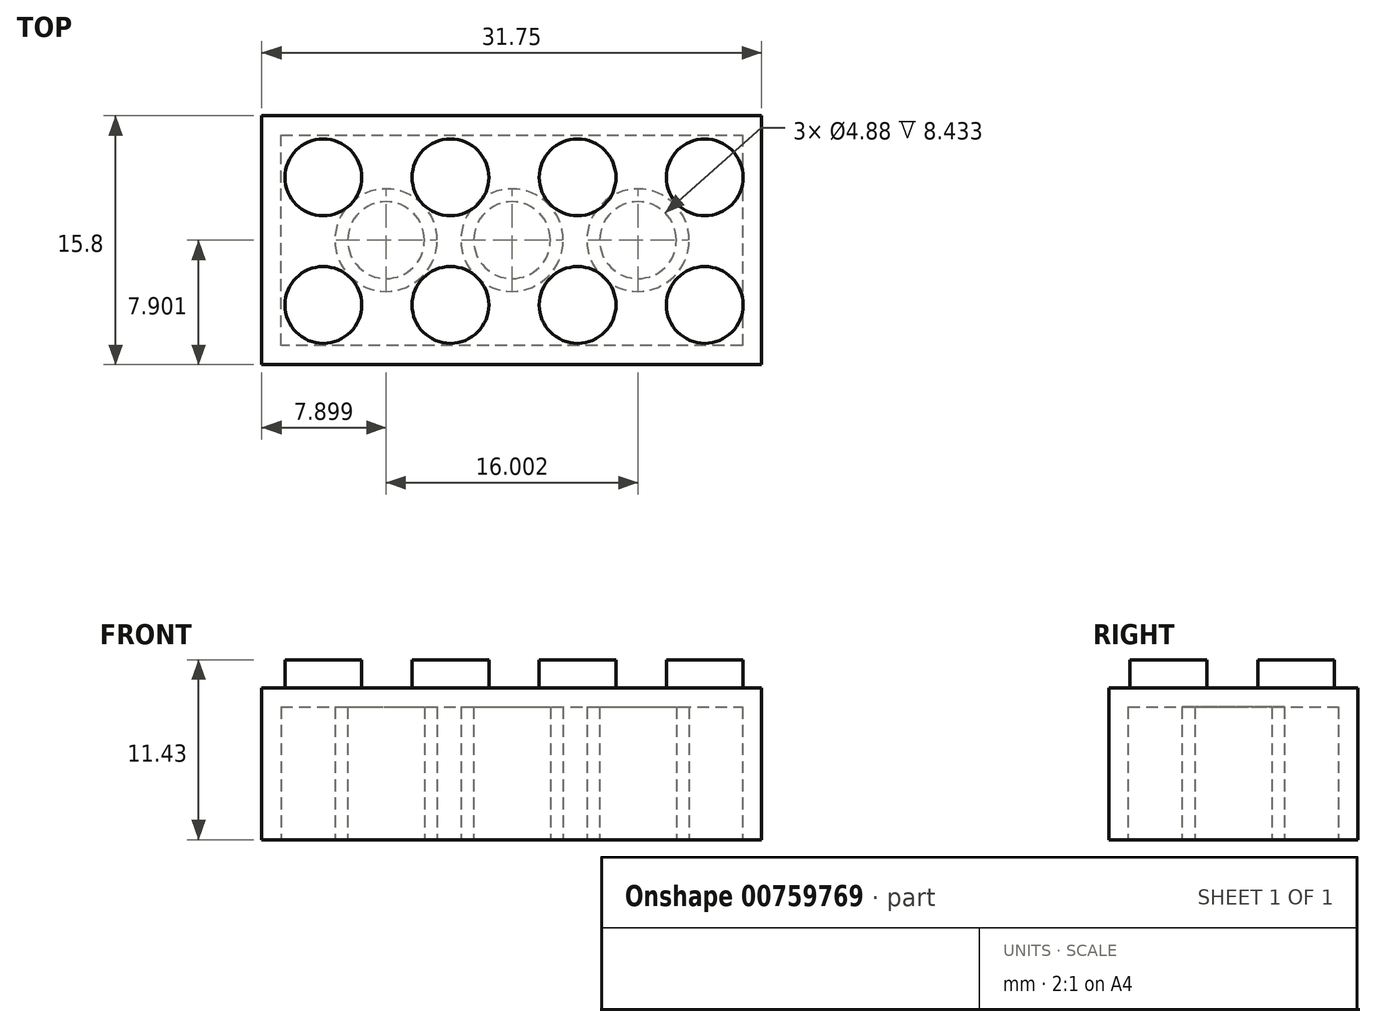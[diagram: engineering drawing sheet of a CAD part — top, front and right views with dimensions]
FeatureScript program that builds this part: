
annotation { "Feature Type Name" : "Feature", "Feature Type Description" : "" }
export const myFeature = defineFeature(function(context is Context, id is Id, definition is map)
    precondition{}
    {
        {
            var Q0;
            Q0=qCreatedBy(makeId("Front.planeOp"),FACE);
            var sketch = newSketch(context, id + "F0", { "sketchPlane" : qUnion([Q0])});
            skLineSegment(sketch, "E0.bottom", {"start": v(0, 0) * mm, "end": v(-31.75, 0) * mm});
            skLineSegment(sketch, "E0.top", {"start": v(0, -9.65) * mm, "end": v(-31.75, -9.65) * mm});
            skLineSegment(sketch, "E0.left", {"start": v(0, 0) * mm, "end": v(0, -9.65) * mm});
            skLineSegment(sketch, "E0.right", {"start": v(-31.75, 0) * mm, "end": v(-31.75, -9.65) * mm});
            skSolve(sketch);
        }
        {
            var Q0;
            Q0 = qSketchRegion(id + "F0", true);
            extrude(context, id + "F1", {"entities" : qUnion([Q0]), "depth" : 15.8 * mm, "offsetDistance" : 25.4 * mm});
        }
        {
            var Q0;
            Q0=makeQuery(id+"F1.opExtrude","SWEPT_FACE",FACE,{"disambiguationData":[OSD([sQuery(id+"F0.wireOp",EDGE,"E0.bottom")])]});
            var sketch = newSketch(context, id + "F2", { "sketchPlane" : qUnion([Q0])});
            skPoint(sketch, "E1.end.orphan", {"position": v(-27.4, 0) * mm});
            skPoint(sketch, "E2.orphan", {"position": v(-27.4, -3.6) * mm});
            skPoint(sketch, "E3.start.orphan", {"position": v(-17.14, -15.98) * mm});
            skPoint(sketch, "E4.orphan", {"position": v(-27.4, -9.8) * mm});
            skPoint(sketch, "E5.end.orphan", {"position": v(-27.4, -15.98) * mm});
            skLineSegment(sketch, "E6.0", {"start": v(0, 0) * mm, "end": v(-31.75, 0) * mm});
            skLineSegment(sketch, "E7.0", {"start": v(-31.75, -15.8) * mm, "end": v(-31.75, 0) * mm});
            skLineSegment(sketch, "E8.0", {"start": v(0, -15.8) * mm, "end": v(-31.75, -15.8) * mm});
            skLineSegment(sketch, "E9.0", {"start": v(0, -15.8) * mm, "end": v(0, 0) * mm});
            skLineSegment(sketch, "E10", {"start": v(-31.75, 0) * mm, "end": v(-27.84, 0) * mm, "construction": true});
            skLineSegment(sketch, "E11", {"start": v(-27.84, 0) * mm, "end": v(-27.84, -15.98) * mm, "construction": true});
            skLineSegment(sketch, "E12", {"start": v(-26.02, 0) * mm, "end": v(-26.02, -3.91) * mm, "construction": true});
            skLineSegment(sketch, "E13", {"start": v(-26.02, -3.91) * mm, "end": v(-31.75, -3.91) * mm, "construction": true});
            skLineSegment(sketch, "E14", {"start": v(-31.75, -3.91) * mm, "end": v(0, -3.91) * mm, "construction": true});
            skCircle(sketch, "E15", {"center": v(-27.84, -3.91) * mm, "radius": 2.44 * mm});
            skCircle(sketch, "E16.1.0.0", {"center": v(-19.76, -3.91) * mm, "radius": 2.44 * mm});
            skCircle(sketch, "E16.2.0.0", {"center": v(-11.68, -3.91) * mm, "radius": 2.44 * mm});
            skCircle(sketch, "E16.3.0.0", {"center": v(-3.6, -3.91) * mm, "radius": 2.44 * mm});
            skLineSegment(sketch, "E16.direction1", {"start": v(-27.84, -3.91) * mm, "end": v(-19.76, -3.91) * mm, "construction": true});
            skCircle(sketch, "E17.1.0.0", {"center": v(-27.84, -12.01) * mm, "radius": 2.44 * mm});
            skCircle(sketch, "E17.1.0.1", {"center": v(-19.76, -12.01) * mm, "radius": 2.44 * mm});
            skCircle(sketch, "E17.1.0.2", {"center": v(-11.68, -12.01) * mm, "radius": 2.44 * mm});
            skCircle(sketch, "E17.1.0.3", {"center": v(-3.6, -12.01) * mm, "radius": 2.44 * mm});
            skLineSegment(sketch, "E17.direction1", {"start": v(-27.84, -3.91) * mm, "end": v(-27.84, -12.01) * mm, "construction": true});
            skSolve(sketch);
        }
        {
            var Q0;
            Q0=makeQuery(id+"F2.imprint","IMPRINT",FACE,{"disambiguationData":[TD([[makeQuery(id+"F2.imprint","IMPRINT",EDGE,{"derivedFrom":sQuery(id+"F2.wireOp",EDGE,"E15")}),1.0]])]});
            var Q1;
            Q1=makeQuery(id+"F2.imprint","IMPRINT",FACE,{"disambiguationData":[TD([[makeQuery(id+"F2.imprint","IMPRINT",EDGE,{"derivedFrom":sQuery(id+"F2.wireOp",EDGE,"E16.1.0.0")}),1.0]])]});
            var Q2;
            Q2=makeQuery(id+"F2.imprint","IMPRINT",FACE,{"disambiguationData":[TD([[makeQuery(id+"F2.imprint","IMPRINT",EDGE,{"derivedFrom":sQuery(id+"F2.wireOp",EDGE,"E16.2.0.0")}),1.0]])]});
            var Q3;
            Q3=makeQuery(id+"F2.imprint","IMPRINT",FACE,{"disambiguationData":[TD([[makeQuery(id+"F2.imprint","IMPRINT",EDGE,{"derivedFrom":sQuery(id+"F2.wireOp",EDGE,"E16.3.0.0")}),1.0]])]});
            var Q4;
            Q4=makeQuery(id+"F2.imprint","IMPRINT",FACE,{"disambiguationData":[TD([[makeQuery(id+"F2.imprint","IMPRINT",EDGE,{"derivedFrom":sQuery(id+"F2.wireOp",EDGE,"E17.1.0.3")}),1.0]])]});
            var Q5;
            Q5=makeQuery(id+"F2.imprint","IMPRINT",FACE,{"disambiguationData":[TD([[makeQuery(id+"F2.imprint","IMPRINT",EDGE,{"derivedFrom":sQuery(id+"F2.wireOp",EDGE,"E17.1.0.2")}),1.0]])]});
            var Q6;
            Q6=makeQuery(id+"F2.imprint","IMPRINT",FACE,{"disambiguationData":[TD([[makeQuery(id+"F2.imprint","IMPRINT",EDGE,{"derivedFrom":sQuery(id+"F2.wireOp",EDGE,"E17.1.0.1")}),1.0]])]});
            var Q7;
            Q7=makeQuery(id+"F2.imprint","IMPRINT",FACE,{"disambiguationData":[TD([[makeQuery(id+"F2.imprint","IMPRINT",EDGE,{"derivedFrom":sQuery(id+"F2.wireOp",EDGE,"E17.1.0.0")}),1.0]])]});
            extrude(context, id + "F3", {"entities" : qUnion([Q0, Q1, Q2, Q3, Q4, Q5, Q6, Q7]), "operationType" : NewBodyOperationType.ADD, "depth" : 1.78 * mm, "offsetDistance" : 25.4 * mm});
        }
        {
            var Q0;
            Q0=makeQuery(id+"F1.opExtrude","SWEPT_FACE",FACE,{"disambiguationData":[OSD([sQuery(id+"F0.wireOp",EDGE,"E0.top")])]});
            var sketch = newSketch(context, id + "F4", { "sketchPlane" : qUnion([Q0])});
            skLineSegment(sketch, "E18.0.0", {"start": v(-31.75, 0) * mm, "end": v(0, 0) * mm});
            skLineSegment(sketch, "E18.0.1", {"start": v(0, 0) * mm, "end": v(0, 15.8) * mm});
            skLineSegment(sketch, "E18.0.2", {"start": v(0, 15.8) * mm, "end": v(-31.75, 15.8) * mm});
            skLineSegment(sketch, "E18.0.3", {"start": v(-31.75, 15.8) * mm, "end": v(-31.75, 0) * mm});
            skLineSegment(sketch, "E19.0", {"start": v(-30.53, 1.22) * mm, "end": v(-1.22, 1.22) * mm});
            skLineSegment(sketch, "E19.1", {"start": v(-30.53, 14.58) * mm, "end": v(-30.53, 1.22) * mm});
            skLineSegment(sketch, "E19.2", {"start": v(-1.22, 14.58) * mm, "end": v(-30.53, 14.58) * mm});
            skLineSegment(sketch, "E19.3", {"start": v(-1.22, 1.22) * mm, "end": v(-1.22, 14.58) * mm});
            skLineSegment(sketch, "E20", {"start": v(-31.75, 7.9) * mm, "end": v(-23.85, 7.9) * mm, "construction": true});
            skLineSegment(sketch, "E21", {"start": v(-27.98, 15.8) * mm, "end": v(-27.98, 7.9) * mm, "construction": true});
            skCircle(sketch, "E22", {"center": v(-23.85, 7.9) * mm, "radius": 2.44 * mm});
            skCircle(sketch, "E23.0", {"center": v(-23.85, 7.9) * mm, "radius": 3.25 * mm});
            skCircle(sketch, "E24.1.0.0", {"center": v(-15.85, 7.9) * mm, "radius": 2.44 * mm});
            skCircle(sketch, "E24.1.0.1", {"center": v(-15.85, 7.9) * mm, "radius": 3.25 * mm});
            skCircle(sketch, "E24.2.0.0", {"center": v(-7.85, 7.9) * mm, "radius": 2.44 * mm});
            skCircle(sketch, "E24.2.0.1", {"center": v(-7.85, 7.9) * mm, "radius": 3.25 * mm});
            skLineSegment(sketch, "E24.direction1", {"start": v(-23.85, 7.9) * mm, "end": v(-15.85, 7.9) * mm, "construction": true});
            skSolve(sketch);
        }
        {
            var Q0;
            Q0=makeQuery(id+"F4.imprint","IMPRINT",FACE,{"disambiguationData":[TD([[makeQuery(id+"F4.imprint","IMPRINT",EDGE,{"derivedFrom":sQuery(id+"F4.wireOp",EDGE,"E19.0")}),1.0]])]});
            var Q1;
            Q1=makeQuery(id+"F4.imprint","IMPRINT",FACE,{"disambiguationData":[TD([[makeQuery(id+"F4.imprint","IMPRINT",EDGE,{"derivedFrom":sQuery(id+"F4.wireOp",EDGE,"E22")}),1.0]])]});
            var Q2;
            Q2=makeQuery(id+"F4.imprint","IMPRINT",FACE,{"disambiguationData":[TD([[makeQuery(id+"F4.imprint","IMPRINT",EDGE,{"derivedFrom":sQuery(id+"F4.wireOp",EDGE,"E24.1.0.0")}),1.0]])]});
            var Q3;
            Q3=makeQuery(id+"F4.imprint","IMPRINT",FACE,{"disambiguationData":[TD([[makeQuery(id+"F4.imprint","IMPRINT",EDGE,{"derivedFrom":sQuery(id+"F4.wireOp",EDGE,"E24.2.0.0")}),1.0]])]});
            extrude(context, id + "F5", {"entities" : qUnion([Q0, Q1, Q2, Q3]), "operationType" : NewBodyOperationType.REMOVE, "oppositeDirection" : true, "depth" : 8.43 * mm, "offsetDistance" : 25.4 * mm});
        }
    });
